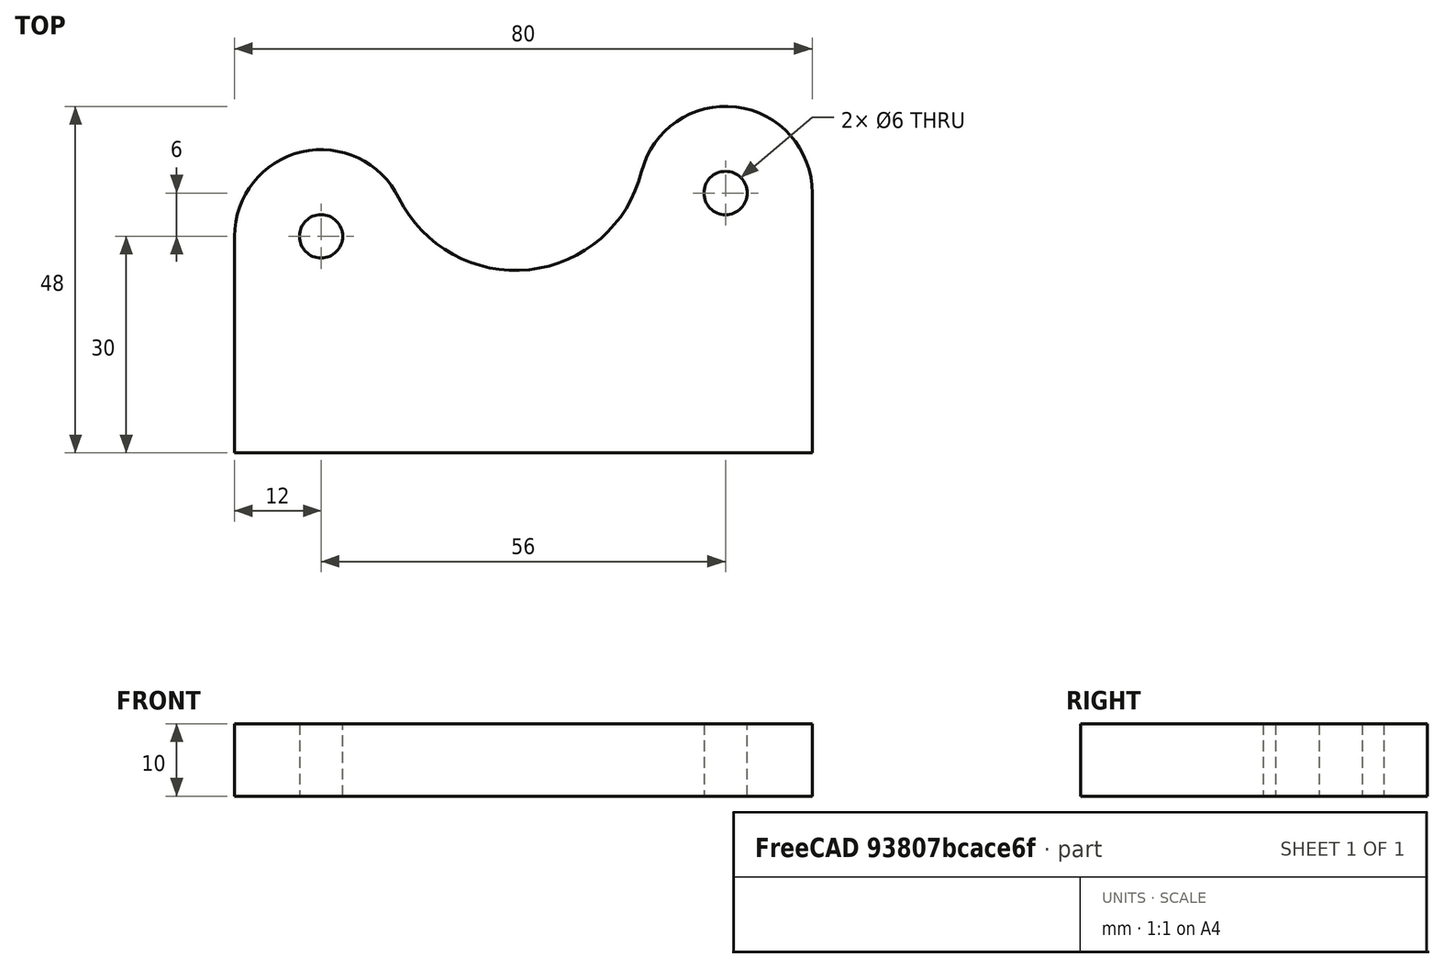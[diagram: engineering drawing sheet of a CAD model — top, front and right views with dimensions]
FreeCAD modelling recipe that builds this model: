
FCSTD DOCUMENT  (FreeCAD 0.19R23756 (Git))
Label: CLAMP_2
License: All rights reserved
LicenseURL: http://en.wikipedia.org/wiki/All_rights_reserved
objects: Sketcher::SketchObject×1, PartDesign::Pad×1, PartDesign::Body×1
note: 4 computed .brp shape members not serialized (recipe doc carries the construction recipe); baked Part::Feature solids carry a one-line shape summary decoded from their .brp

FEATURE [Sketcher::SketchObject] Sketch
  FullyConstrained = true
  MapMode = 5
  Support = -> [XY_Plane]
  sketch-geometry (8):
    g0: LineSegment StartX=0 StartY=0 StartZ=0 EndX=80 EndY=0 EndZ=0
    g1: LineSegment StartX=80 StartY=0 StartZ=0 EndX=80 EndY=36 EndZ=0
    g2: ArcOfCircle CenterX=68 CenterY=36 CenterZ=0 NormalX=0 NormalY=0 NormalZ=1 AngleXU=0 Radius=12 StartAngle=0 EndAngle=2.8963
    g3: ArcOfCircle CenterX=38.898 CenterY=43.2852 CenterZ=0 NormalX=0 NormalY=0 NormalZ=1 AngleXU=0 Radius=18 StartAngle=3.60036 EndAngle=6.03789
    g4: ArcOfCircle CenterX=12 CenterY=30 CenterZ=0 NormalX=0 NormalY=0 NormalZ=1 AngleXU=0 Radius=12 StartAngle=0.458764 EndAngle=3.14159
    g5: LineSegment StartX=0 StartY=30 StartZ=0 EndX=0 EndY=0 EndZ=0
    g6: Circle CenterX=68 CenterY=36 CenterZ=0 NormalX=0 NormalY=0 NormalZ=1 AngleXU=0 Radius=3
    g7: Circle CenterX=12 CenterY=30 CenterZ=0 NormalX=0 NormalY=0 NormalZ=1 AngleXU=0 Radius=3
  constraints (20):
    c: Coincident(g-1,g0)
    c: PointOnObject(g0,g-1)
    c: Coincident(g0,g1)
    c: Vertical(g1)
    c: Tangent(g1,g2) = -1.5708
    c: Tangent(g2,g3) = 1.5708
    c: Tangent(g3,g4) = 1.5708
    c: Tangent(g4,g5) = -1.5708
    c: Coincident(g5,g0)
    c: Vertical(g5)
    c: DistanceX(g4) = 12
    c: DistanceY(g4) = 30
    c: DistanceX(g0,g0) = 80
    c: DistanceY(g1,g1) = 36
    c: Radius(g2) = 12
    c: Coincident(g6,g2)
    c: Diameter(g6) = 6
    c: Coincident(g7,g4)
    c: Diameter(g7) = 6
    c: Radius(g3) = 18
FEATURE [PartDesign::Pad] Pad
  AllowMultiFace = false
  Direction = (1,1,1)
  Length = 10
  Length2 = 100
  Profile = -> Sketch
  Type = 0
FEATURE [PartDesign::Body] Body
  Group = -> [Sketch,Pad]
  Origin = -> Origin
  Tip = -> Pad
